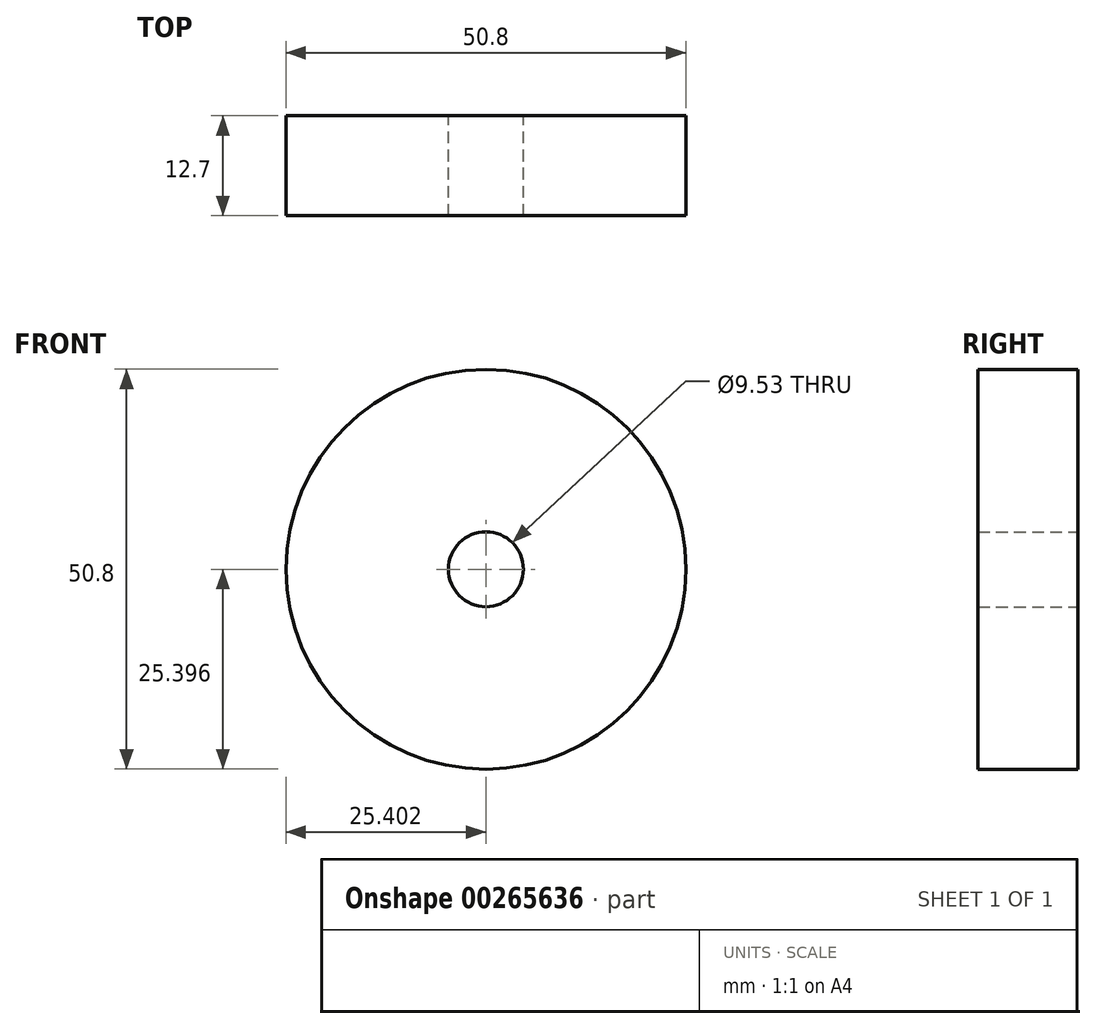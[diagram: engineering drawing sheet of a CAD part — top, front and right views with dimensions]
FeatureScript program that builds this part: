
annotation { "Feature Type Name" : "Feature", "Feature Type Description" : "" }
export const myFeature = defineFeature(function(context is Context, id is Id, definition is map)
    precondition{}
    {
        {
            var Q0;
            Q0=qCreatedBy(makeId("Front.planeOp"),FACE);
            var sketch = newSketch(context, id + "F0", { "sketchPlane" : qUnion([Q0])});
            skCircle(sketch, "E0", {"center": v(42.18, 38.26) * mm, "radius": 25.4 * mm});
            skCircle(sketch, "E1", {"center": v(42.18, 38.26) * mm, "radius": 4.76 * mm});
            skCircle(sketch, "E2.MirrorC", {"center": v(-42.18, 38.26) * mm, "radius": 25.4 * mm});
            skCircle(sketch, "E3.MirrorC", {"center": v(-42.18, 38.26) * mm, "radius": 4.76 * mm});
            skSolve(sketch);
        }
        {
            var Q0;
            Q0=makeQuery(id+"F0.imprint","IMPRINT",FACE,{"disambiguationData":[TD([[makeQuery(id+"F0.imprint","IMPRINT",EDGE,{"derivedFrom":sQuery(id+"F0.wireOp",EDGE,"E2.MirrorC")}),-1.0]])]});
            var Q1;
            Q1=makeQuery(id+"F0.imprint","IMPRINT",FACE,{"disambiguationData":[TD([[makeQuery(id+"F0.imprint","IMPRINT",EDGE,{"derivedFrom":sQuery(id+"F0.wireOp",EDGE,"E0")}),1.0]])]});
            extrude(context, id + "F1", {"entities" : qUnion([Q0, Q1]), "depth" : 12.7 * mm});
        }
    });
